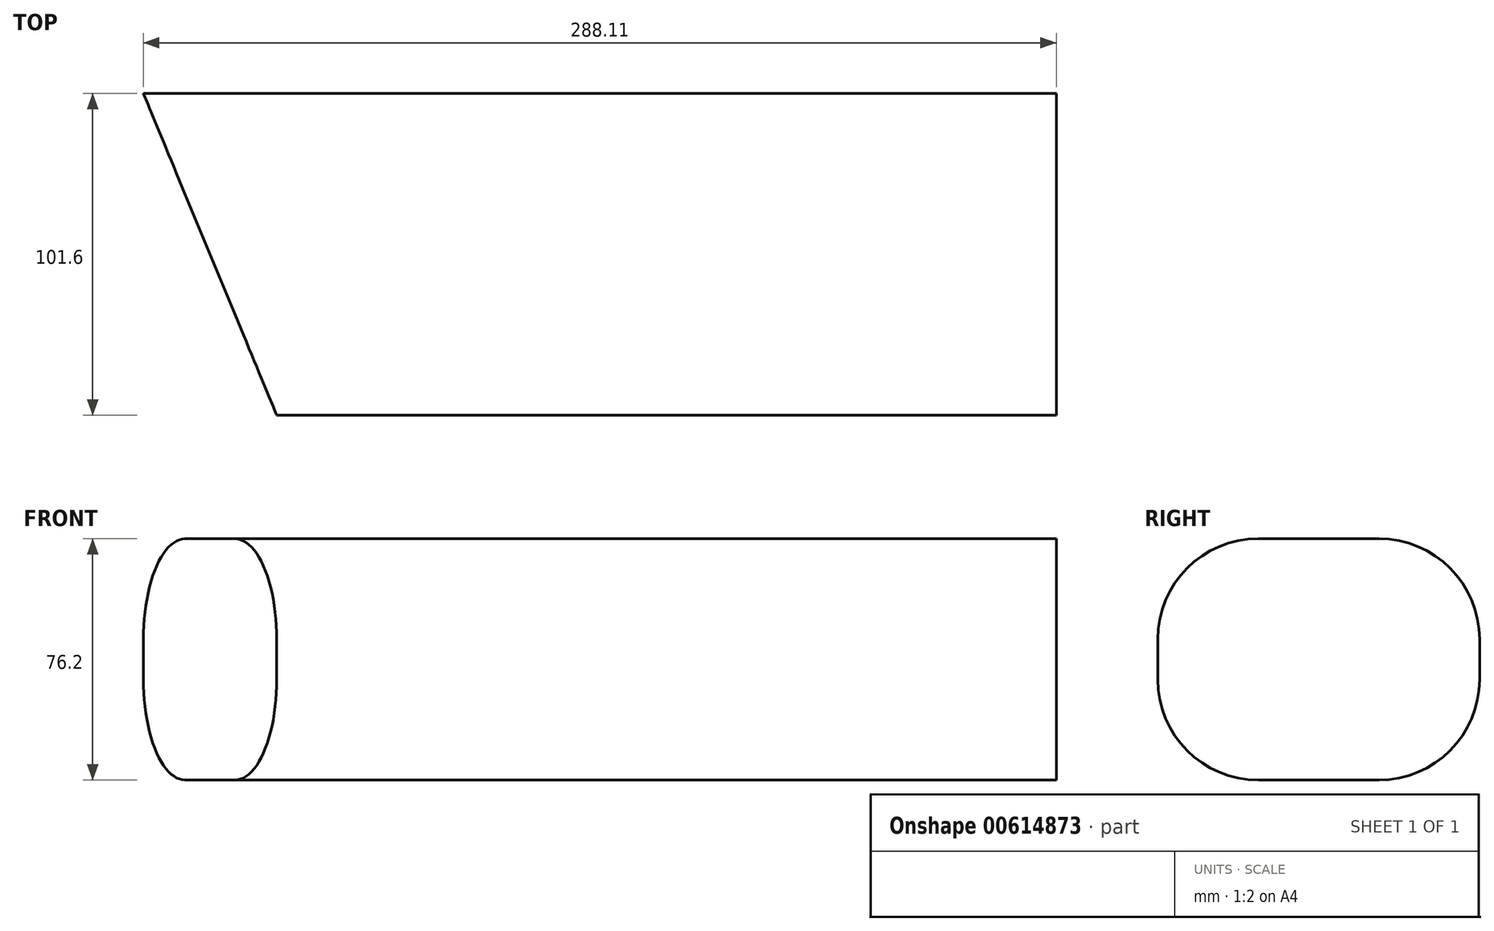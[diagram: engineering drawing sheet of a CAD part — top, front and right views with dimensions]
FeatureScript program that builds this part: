
annotation { "Feature Type Name" : "Feature", "Feature Type Description" : "" }
export const myFeature = defineFeature(function(context is Context, id is Id, definition is map)
    precondition{}
    {
        {
            var Q0;
            Q0=qCreatedBy(makeId("Top.planeOp"),FACE);
            var sketch = newSketch(context, id + "F0", { "sketchPlane" : qUnion([Q0])});
            skLineSegment(sketch, "E0", {"start": v(0, 0) * mm, "end": v(246.03, 0) * mm});
            skLineSegment(sketch, "E1", {"start": v(-42.08, 101.6) * mm, "end": v(0, 0) * mm});
            skLineSegment(sketch, "E2", {"start": v(246.03, 0) * mm, "end": v(246.03, 101.6) * mm});
            skLineSegment(sketch, "E3", {"start": v(-42.08, 101.6) * mm, "end": v(246.03, 101.6) * mm});
            skSolve(sketch);
        }
        {
            var Q0;
            Q0=qSketchRegion(id+"F0",true);
            extrude(context, id + "F1", {"entities" : qUnion([Q0]), "depth" : 76.2 * mm, "offsetDistance" : 25.4 * mm});
        }
        {
            var Q0;
            Q0=makeQuery(id+"F1.opExtrude","CAP_EDGE",EDGE,{"disambiguationData":[OSD([sQuery(id+"F0.wireOp",EDGE,"O834wBZG-Cm29-xfMd-gkqI-FTCGJLI2Fxhv")])],"isStart":false});
            var Q1;
            Q1=makeQuery(id+"F1.opExtrude","CAP_EDGE",EDGE,{"disambiguationData":[OSD([sQuery(id+"F0.wireOp",EDGE,"E0")])],"isStart":false});
            var Q2;
            Q2=makeQuery(id+"F1.opExtrude","CAP_EDGE",EDGE,{"disambiguationData":[OSD([sQuery(id+"F0.wireOp",EDGE,"E0")])],"isStart":true});
            var Q3;
            Q3=makeQuery(id+"F1.opExtrude","CAP_EDGE",EDGE,{"disambiguationData":[OSD([sQuery(id+"F0.wireOp",EDGE,"O834wBZG-Cm29-xfMd-gkqI-FTCGJLI2Fxhv")])],"isStart":true});
            var Q4;
            Q4=makeQuery(id+"F1.opExtrude","CAP_EDGE",EDGE,{"disambiguationData":[OSD([sQuery(id+"F0.wireOp",EDGE,"E3")])],"isStart":false});
            var Q5;
            Q5=makeQuery(id+"F1.opExtrude","CAP_EDGE",EDGE,{"disambiguationData":[OSD([sQuery(id+"F0.wireOp",EDGE,"E3")])],"isStart":true});
            fillet(context, id + "F2", {"entities" : qUnion([Q0, Q1, Q2, Q3, Q4, Q5]), "radius" : 31.75 * mm, "tangentPropagation" : true, "allowEdgeOverflow" : false});
        }
    });
